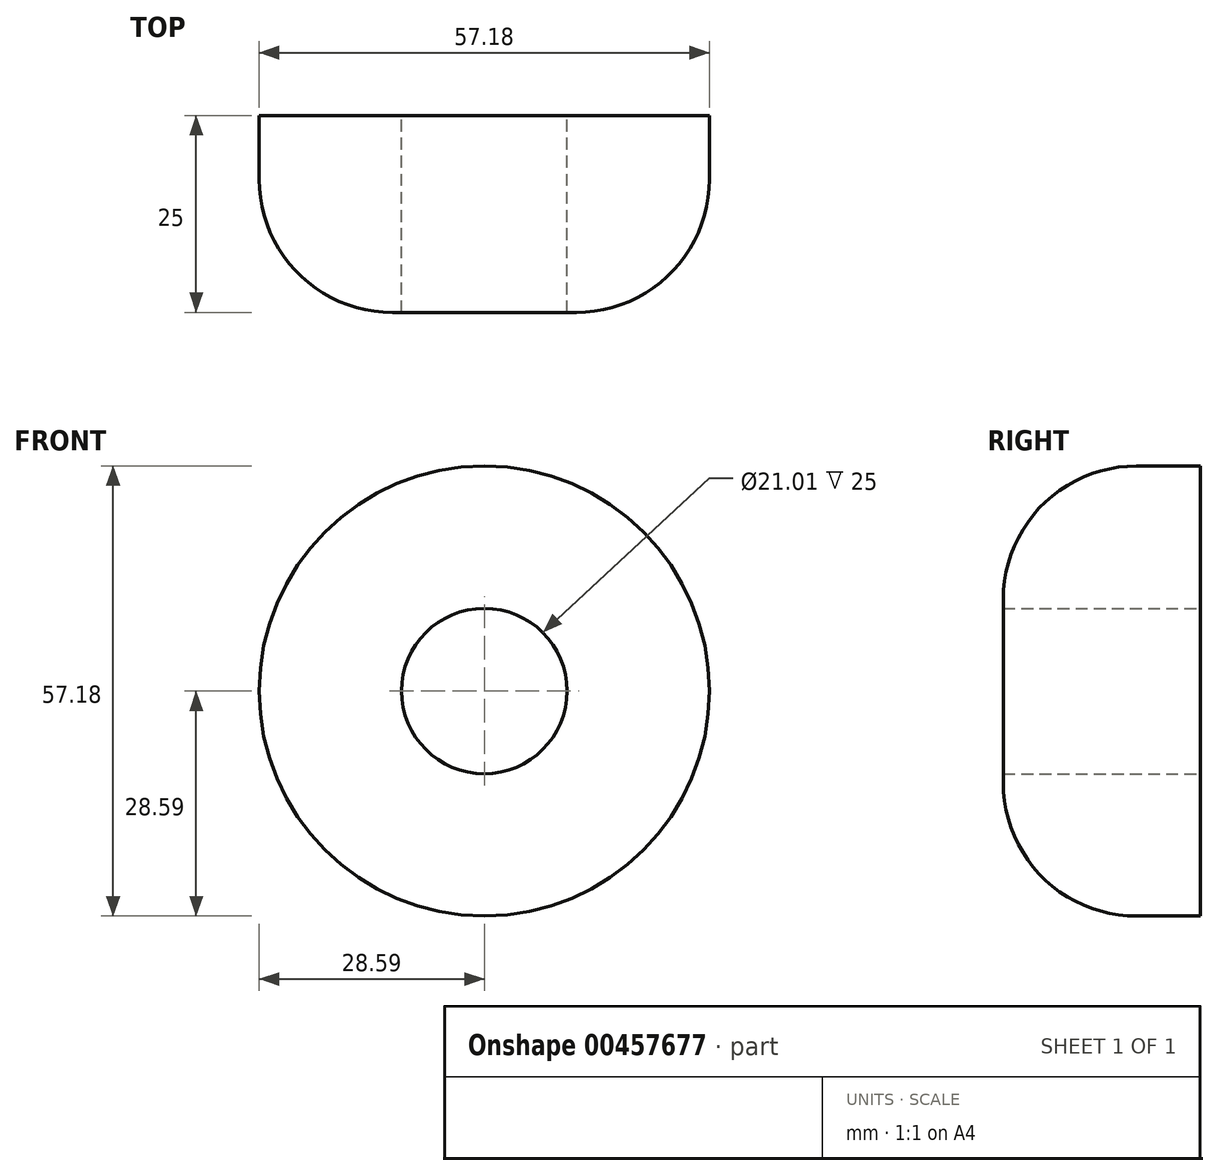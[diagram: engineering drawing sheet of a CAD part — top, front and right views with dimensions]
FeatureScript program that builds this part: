
annotation { "Feature Type Name" : "Feature", "Feature Type Description" : "" }
export const myFeature = defineFeature(function(context is Context, id is Id, definition is map)
    precondition{}
    {
        {
            var Q0;
            Q0=qCreatedBy(makeId("Front.planeOp"),FACE);
            var sketch = newSketch(context, id + "F0", { "sketchPlane" : qUnion([Q0])});
            skCircle(sketch, "E0", {"center": v(0, 0) * mm, "radius": 28.59 * mm});
            skCircle(sketch, "E1", {"center": v(0, 0) * mm, "radius": 10.5 * mm});
            skSolve(sketch);
        }
        {
            var Q0;
            Q0=qSketchRegion(id+"F0",true);
            extrude(context, id + "F1", {"entities" : qUnion([Q0]), "depth" : 25 * mm});
        }
        {
            var Q0;
            Q0=makeQuery(id+"F1.opExtrude","CAP_EDGE",EDGE,{"disambiguationData":[OSD([sQuery(id+"F0.wireOp",EDGE,"E0")])],"isStart":false});
            fillet(context, id + "F2", {"entities" : qUnion([Q0]), "radius" : 16.9 * mm, "tangentPropagation" : true, "allowEdgeOverflow" : false});
        }
    });
